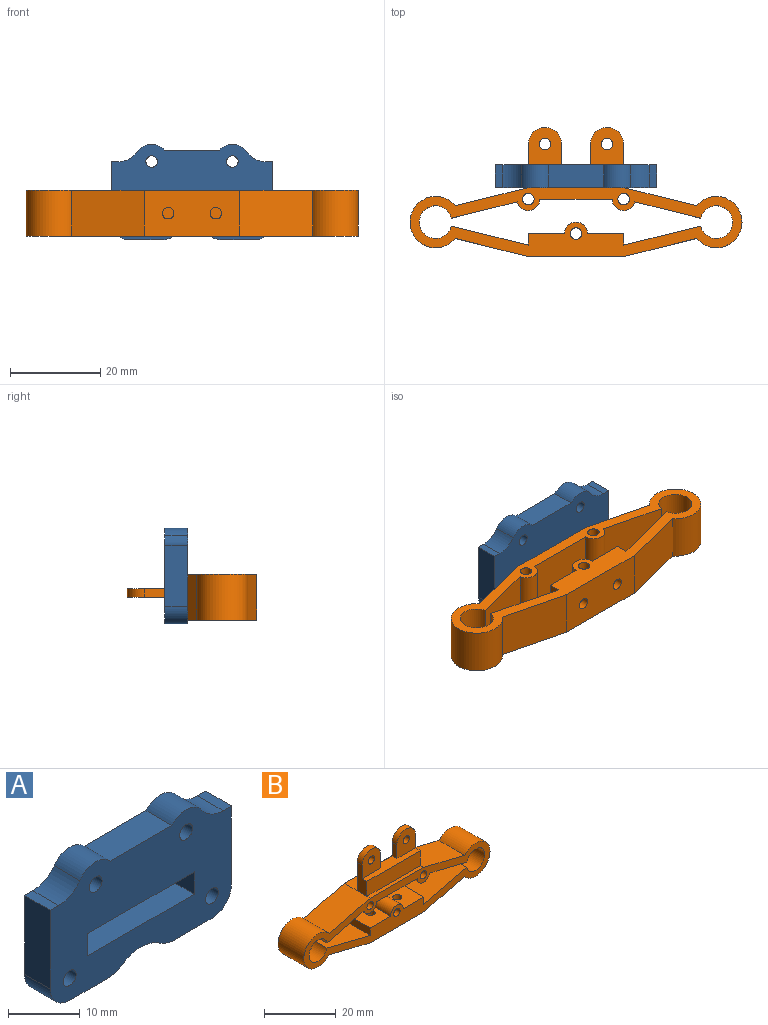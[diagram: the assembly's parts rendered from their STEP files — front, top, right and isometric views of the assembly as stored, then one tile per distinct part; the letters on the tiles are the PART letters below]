
ASSEMBLY  parts=2 mates=1
PART A: 26 faces, bbox 35.7x5.1x21.1 mm
  f0: plane 5.08x1.63mm, normal (0,0,1), area 8.3mm2, adj f10,f12,f13,f14
  f1: cylinder r=3.81mm len=5.97mm, axis (0,1,0), area 34.9mm2, adj f2,f12,f13,f14
  f2: plane 12.16x5.08mm, normal (0,0,1), area 61.8mm2, adj f1,f12,f13,f17
  f3: plane 21.08x5.08mm, normal (0,0,-1), area 107.1mm2, adj f4,f12,f13,f18
  f4: plane 5.08x3.81mm, normal (-1,0,0), area 19.4mm2, adj f3,f5,f12,f13
  f5: plane 21.08x5.08mm, normal (0,0,1), area 107.1mm2, adj f4,f12,f13,f18
  f6: cylinder r=6.35mm len=7.31mm, axis (0,1,0), area 39.6mm2, adj f12,f13,f15,f25
  f7: plane 7.45x5.08mm, normal (0,0,-1), area 37.9mm2, adj f8,f12,f13,f15
  f8: cylinder r=3.81mm len=5.08mm, axis (0,1,0), area 30.4mm2, adj f7,f10,f12,f13
  f9: cylinder r=1.27mm len=5.08mm, axis (0,1,0), area 40.5mm2, adj f12,f13
  f10: plane 13.46x5.08mm, normal (1,0,0), area 68.4mm2, adj f0,f8,f12,f13
  f11: cylinder r=1.27mm len=5.08mm, axis (0,1,0), area 40.5mm2, adj f12,f13
  f12: plane 35.69x21.08mm, normal (0,-1,0), area 571.8mm2, adj f0,f1,f2,f3,f4,f5,f6,f7
  f13: plane 35.69x21.08mm, normal (0,1,0), area 571.8mm2, adj f0,f1,f2,f3,f4,f5,f6,f7
  f14: cylinder r=5.08mm len=5.08mm, axis (0,1,0), area 24.8mm2, adj f0,f1,f12,f13
  f15: cylinder r=5.08mm len=5.08mm, axis (0,1,0), area 15.8mm2, adj f6,f7,f12,f13
  f16: plane 5.08x1.63mm, normal (0,0,1), area 8.3mm2, adj f12,f13,f22,f24
  f17: cylinder r=3.81mm len=5.97mm, axis (0,1,0), area 34.9mm2, adj f2,f12,f13,f24
  f18: plane 5.08x3.81mm, normal (1,0,0), area 19.4mm2, adj f3,f5,f12,f13
  f19: plane 7.45x5.08mm, normal (0,0,-1), area 37.9mm2, adj f12,f13,f20,f25
  f20: cylinder r=3.81mm len=5.08mm, axis (0,1,0), area 30.4mm2, adj f12,f13,f19,f22
  f21: cylinder r=1.27mm len=5.08mm, axis (0,1,0), area 40.5mm2, adj f12,f13
  f22: plane 13.46x5.08mm, normal (-1,0,0), area 68.4mm2, adj f12,f13,f16,f20
  f23: cylinder r=1.27mm len=5.08mm, axis (0,1,0), area 40.5mm2, adj f12,f13
  f24: cylinder r=5.08mm len=5.08mm, axis (0,1,0), area 24.8mm2, adj f12,f13,f16,f17
  f25: cylinder r=5.08mm len=5.08mm, axis (0,1,0), area 15.8mm2, adj f6,f12,f13,f19
PART B: 43 faces, bbox 73.4x10.2x28.6 mm
  f0: plane 4.57x1.91mm, normal (1,0,0), area 8.7mm2, adj f1,f4,f5,f6
  f1: cylinder r=3.68mm len=7.37mm, axis (0,1,0), area 22mm2, adj f0,f2,f4,f5
  f2: plane 9.65x3.81mm, normal (-1,0,0), area 28.1mm2, adj f1,f4,f5,f6,f7,f10
  f3: cylinder r=1.27mm len=2.54mm, axis (0,1,0), area 15.2mm2, adj f4,f5
  f4: plane 8.26x7.37mm, normal (0,-1,0), area 49.9mm2, adj f0,f1,f2,f3,f6
  f5: plane 21.08x13.34mm, normal (0,1,0), area 206.9mm2, adj f0,f1,f2,f3,f6,f9,f27,f28
  f6: plane 21.08x3.81mm, normal (0,0,1), area 52.3mm2, adj f0,f2,f4,f5,f7,f27,f29,f31
  f7: plane 21.08x5.08mm, normal (0,-1,0), area 107.1mm2, adj f2,f6,f8,f29
  f8: plane 21.08x1.27mm, normal (0,0,1), area 26.8mm2, adj f7,f10,f24,f32
  f9: plane 21.08x5.08mm, normal (0,0,1), area 107.1mm2, adj f5,f10,f25,f32
  f10: plane 16.14x10.16mm, normal (-0.24,0,0.97), area 169mm2, adj f2,f8,f9,f11,f24,f25
  f11: cylinder r=5.67mm len=11.33mm, axis (0,1,0), area 281.9mm2, adj f10,f12,f24,f25
  f12: plane 16.14x10.16mm, normal (-0.24,0,-0.97), area 169mm2, adj f11,f13,f24,f25
  f13: plane 21.08x10.16mm, normal (0,0,-1), area 204.1mm2, adj f12,f24,f25,f26,f34,f42
  f14: cylinder r=2.54mm len=10.16mm, axis (0,1,0), area 81.1mm2, adj f15,f24,f25,f35
  f15: plane 10.16x8mm, normal (0,0,1), area 76.2mm2, adj f14,f16,f24,f25,f26
  f16: plane 10.16x2.54mm, normal (-1,0,0), area 25.8mm2, adj f15,f17,f24,f25
  f17: plane 17x10.16mm, normal (0.24,0,0.97), area 177.9mm2, adj f16,f18,f24,f25
  f18: cylinder r=3.61mm len=10.16mm, axis (0,1,0), area 212.5mm2, adj f17,f19,f24,f25
  f19: plane 14.53x10.16mm, normal (0.24,0,-0.97), area 152.1mm2, adj f18,f20,f24,f25
  f20: cylinder r=2.54mm len=10.16mm, axis (0,1,0), area 74.8mm2, adj f19,f21,f24,f25
  f21: plane 16x10.16mm, normal (0,0,-1), area 162.6mm2, adj f20,f24,f25,f40
  f22: cylinder r=1.27mm len=10.16mm, axis (0,1,0), area 81.1mm2, adj f24,f25
  f23: cylinder r=1.27mm len=10.16mm, axis (0,1,0), area 81.1mm2, adj f24,f25
  f24: plane 73.41x15.24mm, normal (0,-1,0), area 442.1mm2, adj f8,f10,f11,f12,f13,f14,f15,f16
  f25: plane 73.41x15.24mm, normal (0,1,0), area 442.1mm2, adj f9,f10,f11,f12,f13,f14,f15,f16
  f26: cylinder r=1.27mm len=5.08mm, axis (0,0,-1), area 40.5mm2, adj f13,f15
  f27: plane 4.57x1.91mm, normal (-1,0,0), area 8.7mm2, adj f5,f6,f28,f31
  f28: cylinder r=3.68mm len=7.37mm, axis (0,1,0), area 22mm2, adj f5,f27,f29,f31
  f29: plane 9.65x3.81mm, normal (1,0,0), area 28.1mm2, adj f5,f6,f7,f28,f31,f32
  f30: cylinder r=1.27mm len=2.54mm, axis (0,1,0), area 15.2mm2, adj f5,f31
  f31: plane 8.26x7.37mm, normal (0,-1,0), area 49.9mm2, adj f6,f27,f28,f29,f30
  f32: plane 16.14x10.16mm, normal (0.24,0,0.97), area 169mm2, adj f8,f9,f24,f25,f29,f33
  f33: cylinder r=5.67mm len=11.33mm, axis (0,1,0), area 281.9mm2, adj f24,f25,f32,f34
  f34: plane 16.14x10.16mm, normal (0.24,0,-0.97), area 169mm2, adj f13,f24,f25,f33
  f35: plane 10.16x8mm, normal (0,0,1), area 76.2mm2, adj f14,f24,f25,f36,f42
  f36: plane 10.16x2.54mm, normal (1,0,0), area 25.8mm2, adj f24,f25,f35,f37
  f37: plane 17x10.16mm, normal (-0.24,0,0.97), area 177.9mm2, adj f24,f25,f36,f38
  f38: cylinder r=3.61mm len=10.16mm, axis (0,1,0), area 212.5mm2, adj f24,f25,f37,f39
  f39: plane 14.53x10.16mm, normal (-0.24,0,-0.97), area 152.1mm2, adj f24,f25,f38,f40
  f40: cylinder r=2.54mm len=10.16mm, axis (0,1,0), area 74.8mm2, adj f21,f24,f25,f39
  f41: cylinder r=1.27mm len=10.16mm, axis (0,1,0), area 81.1mm2, adj f24,f25
  f42: cylinder r=1.27mm len=5.08mm, axis (0,0,-1), area 40.5mm2, adj f13,f35
PLACE A t=(-20.51,-3.11,2.56)mm
PLACE B rot(axis=(-1,0,0),90deg) t=(-20.51,-3.11,4.59)mm
MATE fastened B.f7 <-> A.f3  axis (0,0,1) through (-20.51,-5.65,8.4)mm
